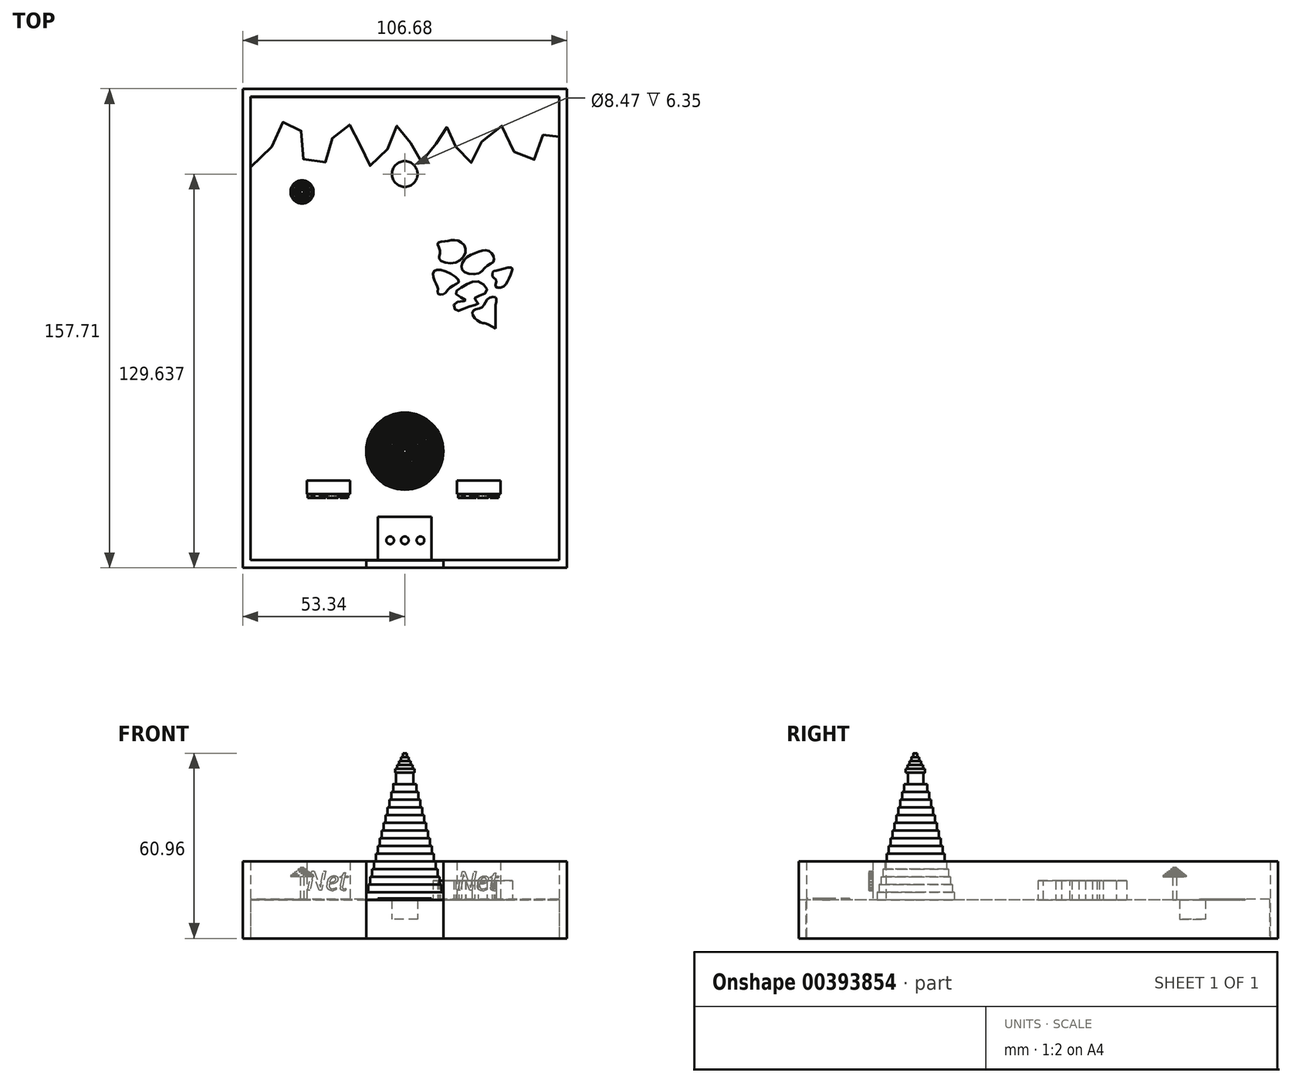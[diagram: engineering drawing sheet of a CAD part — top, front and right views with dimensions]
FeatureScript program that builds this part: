
annotation { "Feature Type Name" : "Feature", "Feature Type Description" : "" }
export const myFeature = defineFeature(function(context is Context, id is Id, definition is map)
    precondition{}
    {
        {
            var Q0;
            Q0=qCreatedBy(makeId("Top.planeOp"),FACE);
            var sketch = newSketch(context, id + "F0", { "sketchPlane" : qUnion([Q0])});
            skLineSegment(sketch, "E0.bottom", {"start": v(0, 0) * mm, "end": v(-50.8, 0) * mm});
            skLineSegment(sketch, "E0.top", {"start": v(0, -76.2) * mm, "end": v(-50.8, -76.2) * mm});
            skLineSegment(sketch, "E0.left", {"start": v(0, 0) * mm, "end": v(0, -76.2) * mm});
            skLineSegment(sketch, "E0.right", {"start": v(-50.8, 0) * mm, "end": v(-50.8, -76.2) * mm});
            skLineSegment(sketch, "E1.top", {"start": v(0, 76.2) * mm, "end": v(-50.8, 76.2) * mm});
            skLineSegment(sketch, "E1.left", {"start": v(0, 0) * mm, "end": v(0, 76.2) * mm});
            skLineSegment(sketch, "E1.right", {"start": v(-50.8, 0) * mm, "end": v(-50.8, 76.2) * mm});
            skLineSegment(sketch, "E2.bottom", {"start": v(0, 0) * mm, "end": v(50.8, 0) * mm});
            skLineSegment(sketch, "E2.top", {"start": v(0, 76.2) * mm, "end": v(50.8, 76.2) * mm});
            skLineSegment(sketch, "E2.right", {"start": v(50.8, 0) * mm, "end": v(50.8, 76.2) * mm});
            skLineSegment(sketch, "E3.top", {"start": v(0, -76.2) * mm, "end": v(50.8, -76.2) * mm});
            skLineSegment(sketch, "E3.right", {"start": v(50.8, 0) * mm, "end": v(50.8, -76.2) * mm});
            skLineSegment(sketch, "E4", {"start": v(0, 76.2) * mm, "end": v(0, -76.2) * mm, "construction": true});
            skCircle(sketch, "E5", {"center": v(0, 50.9) * mm, "radius": 4.23 * mm});
            skSolve(sketch);
        }
        {
            var Q0;
            Q0=makeQuery(id+"F0.imprint","IMPRINT",FACE,{"disambiguationData":[TD([[makeQuery(id+"F0.imprint","IMPRINT",EDGE,{"derivedFrom":sQuery(id+"F0.wireOp",EDGE,"E0.top")}),-1.0]])]});
            var Q1;
            Q1=makeQuery(id+"F0.imprint","IMPRINT",FACE,{"disambiguationData":[TD([[makeQuery(id+"F0.imprint","IMPRINT",EDGE,{"derivedFrom":sQuery(id+"F0.wireOp",EDGE,"E2.bottom")}),-1.0]])]});
            var Q2;
            {var subQ1=sQuery(id+"F0.wireOp",EDGE,"E0.bottom");Q2=makeQuery(id+"F0.imprint","IMPRINT",FACE,{"disambiguationData":[TD([[makeQuery(id+"F0.imprint","IMPRINT",EDGE,{"derivedFrom":subQ1}),-1.0]])]});}
            var Q3;
            {var subQ1=sQuery(id+"F0.wireOp",EDGE,"E2.top");Q3=makeQuery(id+"F0.imprint","IMPRINT",FACE,{"disambiguationData":[TD([[makeQuery(id+"F0.imprint","IMPRINT",EDGE,{"derivedFrom":subQ1}),-1.0]])]});}
            extrude(context, id + "F1", {"entities" : qUnion([Q0, Q1, Q2, Q3]), "depth" : 12.7 * mm});
        }
        {
            var Q0;
            Q0=makeQuery(id+"F1.opExtrude","CAP_FACE",FACE,{"disambiguationData":[OSD([sQuery(id+"F0.wireOp",EDGE,"E0.top"),sQuery(id+"F0.wireOp",EDGE,"E0.right"),sQuery(id+"F0.wireOp",EDGE,"E1.top"),sQuery(id+"F0.wireOp",EDGE,"E1.right"),sQuery(id+"F0.wireOp",EDGE,"E2.top"),sQuery(id+"F0.wireOp",EDGE,"E2.right"),sQuery(id+"F0.wireOp",EDGE,"E3.top"),sQuery(id+"F0.wireOp",EDGE,"E3.right")])],"isStart":false});
            var sketch = newSketch(context, id + "F2", { "sketchPlane" : qUnion([Q0])});
            skCircle(sketch, "E6", {"center": v(0, -40.32) * mm, "radius": 12.7 * mm});
            skSolve(sketch);
        }
        {
            var Q0;
            Q0 = qSketchRegion(id + "F2", true);
            extrude(context, id + "F3", {"entities" : qUnion([Q0]), "operationType" : NewBodyOperationType.ADD, "depth" : 2.54 * mm});
        }
        {
            var Q0;
            Q0=makeQuery(id+"F3.opExtrude","CAP_FACE",FACE,{"disambiguationData":[OSD([sQuery(id+"F2.wireOp",EDGE,"E6")])],"isStart":false});
            var sketch = newSketch(context, id + "F4", { "sketchPlane" : qUnion([Q0])});
            skCircle(sketch, "E7", {"center": v(0, -40.32) * mm, "radius": 12.07 * mm});
            skSolve(sketch);
        }
        {
            var Q0;
            Q0 = qSketchRegion(id + "F4", true);
            extrude(context, id + "F5", {"entities" : qUnion([Q0]), "operationType" : NewBodyOperationType.ADD, "depth" : 2.54 * mm});
        }
        {
            var Q0;
            Q0=makeQuery(id+"F5.opExtrude","CAP_FACE",FACE,{"disambiguationData":[OSD([sQuery(id+"F4.wireOp",EDGE,"E7")])],"isStart":false});
            var sketch = newSketch(context, id + "F6", { "sketchPlane" : qUnion([Q0])});
            skCircle(sketch, "E8", {"center": v(0, -40.32) * mm, "radius": 11.43 * mm});
            skSolve(sketch);
        }
        {
            var Q0;
            Q0 = qSketchRegion(id + "F6", true);
            extrude(context, id + "F7", {"entities" : qUnion([Q0]), "operationType" : NewBodyOperationType.ADD, "depth" : 2.54 * mm});
        }
        {
            var Q0;
            Q0=makeQuery(id+"F7.opExtrude","CAP_FACE",FACE,{"disambiguationData":[OSD([sQuery(id+"F6.wireOp",EDGE,"E8")])],"isStart":false});
            var sketch = newSketch(context, id + "F8", { "sketchPlane" : qUnion([Q0])});
            skCircle(sketch, "E9", {"center": v(0, -40.32) * mm, "radius": 10.8 * mm});
            skSolve(sketch);
        }
        {
            var Q0;
            Q0 = qSketchRegion(id + "F8", true);
            extrude(context, id + "F9", {"entities" : qUnion([Q0]), "operationType" : NewBodyOperationType.ADD, "depth" : 2.54 * mm});
        }
        {
            var Q0;
            Q0=makeQuery(id+"F9.opExtrude","CAP_FACE",FACE,{"disambiguationData":[OSD([sQuery(id+"F8.wireOp",EDGE,"E9")])],"isStart":false});
            var sketch = newSketch(context, id + "F10", { "sketchPlane" : qUnion([Q0])});
            skCircle(sketch, "E10", {"center": v(0, -40.32) * mm, "radius": 10.16 * mm});
            skSolve(sketch);
        }
        {
            var Q0;
            Q0 = qSketchRegion(id + "F10", true);
            extrude(context, id + "F11", {"entities" : qUnion([Q0]), "operationType" : NewBodyOperationType.ADD, "depth" : 2.54 * mm});
        }
        {
            var Q0;
            Q0=makeQuery(id+"F11.opExtrude","CAP_FACE",FACE,{"disambiguationData":[OSD([sQuery(id+"F10.wireOp",EDGE,"E10")])],"isStart":false});
            var sketch = newSketch(context, id + "F12", { "sketchPlane" : qUnion([Q0])});
            skCircle(sketch, "E11", {"center": v(0, -40.32) * mm, "radius": 9.53 * mm});
            skSolve(sketch);
        }
        {
            var Q0;
            Q0 = qSketchRegion(id + "F12", true);
            extrude(context, id + "F13", {"entities" : qUnion([Q0]), "operationType" : NewBodyOperationType.ADD, "depth" : 2.54 * mm});
        }
        {
            var Q0;
            Q0=makeQuery(id+"F13.opExtrude","CAP_FACE",FACE,{"disambiguationData":[OSD([sQuery(id+"F12.wireOp",EDGE,"E11")])],"isStart":false});
            var sketch = newSketch(context, id + "F14", { "sketchPlane" : qUnion([Q0])});
            skCircle(sketch, "E12", {"center": v(0, -40.32) * mm, "radius": 8.89 * mm});
            skSolve(sketch);
        }
        {
            var Q0;
            Q0 = qSketchRegion(id + "F14", true);
            extrude(context, id + "F15", {"entities" : qUnion([Q0]), "operationType" : NewBodyOperationType.ADD, "depth" : 2.54 * mm});
        }
        {
            var Q0;
            Q0=makeQuery(id+"F15.opExtrude","CAP_FACE",FACE,{"disambiguationData":[OSD([sQuery(id+"F14.wireOp",EDGE,"E12")])],"isStart":false});
            var sketch = newSketch(context, id + "F16", { "sketchPlane" : qUnion([Q0])});
            skCircle(sketch, "E13", {"center": v(0, -40.32) * mm, "radius": 8.26 * mm});
            skSolve(sketch);
        }
        {
            var Q0;
            Q0 = qSketchRegion(id + "F16", true);
            extrude(context, id + "F17", {"entities" : qUnion([Q0]), "operationType" : NewBodyOperationType.ADD, "depth" : 2.54 * mm});
        }
        {
            var Q0;
            Q0=makeQuery(id+"F17.opExtrude","CAP_FACE",FACE,{"disambiguationData":[OSD([sQuery(id+"F16.wireOp",EDGE,"E13")])],"isStart":false});
            var sketch = newSketch(context, id + "F18", { "sketchPlane" : qUnion([Q0])});
            skCircle(sketch, "E14", {"center": v(0, -40.32) * mm, "radius": 7.62 * mm});
            skSolve(sketch);
        }
        {
            var Q0;
            Q0 = qSketchRegion(id + "F18", true);
            extrude(context, id + "F19", {"entities" : qUnion([Q0]), "operationType" : NewBodyOperationType.ADD, "depth" : 2.54 * mm});
        }
        {
            var Q0;
            Q0=makeQuery(id+"F19.opExtrude","CAP_FACE",FACE,{"disambiguationData":[OSD([sQuery(id+"F18.wireOp",EDGE,"E14")])],"isStart":false});
            var sketch = newSketch(context, id + "F20", { "sketchPlane" : qUnion([Q0])});
            skCircle(sketch, "E15", {"center": v(0, -40.32) * mm, "radius": 6.99 * mm});
            skSolve(sketch);
        }
        {
            var Q0;
            Q0 = qSketchRegion(id + "F20", true);
            extrude(context, id + "F21", {"entities" : qUnion([Q0]), "operationType" : NewBodyOperationType.ADD, "depth" : 2.54 * mm});
        }
        {
            var Q0;
            Q0=makeQuery(id+"F21.opExtrude","CAP_FACE",FACE,{"disambiguationData":[OSD([sQuery(id+"F20.wireOp",EDGE,"E15")])],"isStart":false});
            var sketch = newSketch(context, id + "F22", { "sketchPlane" : qUnion([Q0])});
            skCircle(sketch, "E16", {"center": v(0, -40.32) * mm, "radius": 6.35 * mm});
            skSolve(sketch);
        }
        {
            var Q0;
            Q0 = qSketchRegion(id + "F22", true);
            extrude(context, id + "F23", {"entities" : qUnion([Q0]), "operationType" : NewBodyOperationType.ADD, "depth" : 2.54 * mm});
        }
        {
            var Q0;
            Q0=makeQuery(id+"F23.opExtrude","CAP_FACE",FACE,{"disambiguationData":[OSD([sQuery(id+"F22.wireOp",EDGE,"E16")])],"isStart":false});
            var sketch = newSketch(context, id + "F24", { "sketchPlane" : qUnion([Q0])});
            skCircle(sketch, "E17", {"center": v(0, -40.32) * mm, "radius": 5.72 * mm});
            skSolve(sketch);
        }
        {
            var Q0;
            Q0 = qSketchRegion(id + "F24", true);
            extrude(context, id + "F25", {"entities" : qUnion([Q0]), "operationType" : NewBodyOperationType.ADD, "depth" : 2.54 * mm});
        }
        {
            var Q0;
            Q0=makeQuery(id+"F25.opExtrude","CAP_FACE",FACE,{"disambiguationData":[OSD([sQuery(id+"F24.wireOp",EDGE,"E17")])],"isStart":false});
            var sketch = newSketch(context, id + "F26", { "sketchPlane" : qUnion([Q0])});
            skCircle(sketch, "E18", {"center": v(0, -40.32) * mm, "radius": 5.08 * mm});
            skSolve(sketch);
        }
        {
            var Q0;
            Q0 = qSketchRegion(id + "F26", true);
            extrude(context, id + "F27", {"entities" : qUnion([Q0]), "operationType" : NewBodyOperationType.ADD, "depth" : 2.54 * mm});
        }
        {
            var Q0;
            Q0=makeQuery(id+"F27.opExtrude","CAP_FACE",FACE,{"disambiguationData":[OSD([sQuery(id+"F26.wireOp",EDGE,"E18")])],"isStart":false});
            var sketch = newSketch(context, id + "F28", { "sketchPlane" : qUnion([Q0])});
            skCircle(sketch, "E19", {"center": v(0, -40.32) * mm, "radius": 4.45 * mm});
            skSolve(sketch);
        }
        {
            var Q0;
            Q0 = qSketchRegion(id + "F28", true);
            extrude(context, id + "F29", {"entities" : qUnion([Q0]), "operationType" : NewBodyOperationType.ADD, "depth" : 2.54 * mm});
        }
        {
            var Q0;
            Q0=makeQuery(id+"F29.opExtrude","CAP_FACE",FACE,{"disambiguationData":[OSD([sQuery(id+"F28.wireOp",EDGE,"E19")])],"isStart":false});
            var sketch = newSketch(context, id + "F30", { "sketchPlane" : qUnion([Q0])});
            skCircle(sketch, "E20", {"center": v(0, -40.32) * mm, "radius": 3.81 * mm});
            skSolve(sketch);
        }
        {
            var Q0;
            Q0 = qSketchRegion(id + "F30", true);
            extrude(context, id + "F31", {"entities" : qUnion([Q0]), "operationType" : NewBodyOperationType.ADD, "depth" : 2.54 * mm});
        }
        {
            var Q0;
            Q0=makeQuery(id+"F31.opExtrude","CAP_FACE",FACE,{"disambiguationData":[OSD([sQuery(id+"F30.wireOp",EDGE,"E20")])],"isStart":false});
            var sketch = newSketch(context, id + "F32", { "sketchPlane" : qUnion([Q0])});
            skSolve(sketch);
        }
        {
            var Q0;
            Q0=makeQuery(id+"F32.imprint","IMPRINT",FACE,{"disambiguationData":[TD([[makeQuery(id+"F32.imprint","IMPRINT",EDGE,{"derivedFrom":makeQuery(id+"F31.opExtrude","CAP_EDGE",EDGE,{"disambiguationData":[OSD([sQuery(id+"F30.wireOp",EDGE,"E20")])],"isStart":false})}),1.0]])]});
            var sketch = newSketch(context, id + "F33", { "sketchPlane" : qUnion([Q0])});
            skLineSegment(sketch, "E21.bottom", {"start": v(2.78, -37.78) * mm, "end": v(-2.9, -37.78) * mm});
            skLineSegment(sketch, "E21.top", {"start": v(2.78, -42.86) * mm, "end": v(-2.9, -42.86) * mm});
            skLineSegment(sketch, "E21.left", {"start": v(-2.9, -42.86) * mm, "end": v(-2.9, -37.78) * mm});
            skLineSegment(sketch, "E21.right", {"start": v(2.78, -42.86) * mm, "end": v(2.78, -37.78) * mm});
            skSolve(sketch);
        }
        {
            var Q0;
            Q0 = qSketchRegion(id + "F33", true);
            extrude(context, id + "F34", {"entities" : qUnion([Q0]), "operationType" : NewBodyOperationType.ADD, "depth" : 3.8 * mm});
        }
        {
            var Q0;
            Q0=makeQuery(id+"F34.opExtrude","CAP_FACE",FACE,{"disambiguationData":[OSD([sQuery(id+"F33.wireOp",EDGE,"E21.bottom"),sQuery(id+"F33.wireOp",EDGE,"E21.top"),sQuery(id+"F33.wireOp",EDGE,"E21.left"),sQuery(id+"F33.wireOp",EDGE,"E21.right")])],"isStart":false});
            var sketch = newSketch(context, id + "F35", { "sketchPlane" : qUnion([Q0])});
            skCircle(sketch, "E22", {"center": v(0, -40.36) * mm, "radius": 3.17 * mm});
            skSolve(sketch);
        }
        {
            var Q0;
            Q0 = qSketchRegion(id + "F35", true);
            extrude(context, id + "F36", {"entities" : qUnion([Q0]), "operationType" : NewBodyOperationType.ADD, "depth" : 1.27 * mm});
        }
        {
            var Q0;
            Q0=makeQuery(id+"F36.opExtrude","CAP_FACE",FACE,{"disambiguationData":[OSD([sQuery(id+"F35.wireOp",EDGE,"E22")])],"isStart":false});
            var sketch = newSketch(context, id + "F37", { "sketchPlane" : qUnion([Q0])});
            skCircle(sketch, "E23", {"center": v(0, -40.36) * mm, "radius": 2.54 * mm});
            skSolve(sketch);
        }
        {
            var Q0;
            Q0 = qSketchRegion(id + "F37", true);
            extrude(context, id + "F38", {"entities" : qUnion([Q0]), "operationType" : NewBodyOperationType.ADD, "depth" : 1.27 * mm});
        }
        {
            var Q0;
            Q0=makeQuery(id+"F38.opExtrude","CAP_FACE",FACE,{"disambiguationData":[OSD([sQuery(id+"F37.wireOp",EDGE,"E23")])],"isStart":false});
            var sketch = newSketch(context, id + "F39", { "sketchPlane" : qUnion([Q0])});
            skCircle(sketch, "E24", {"center": v(0, -40.36) * mm, "radius": 1.9 * mm});
            skSolve(sketch);
        }
        {
            var Q0;
            Q0 = qSketchRegion(id + "F39", true);
            extrude(context, id + "F40", {"entities" : qUnion([Q0]), "operationType" : NewBodyOperationType.ADD, "depth" : 1.27 * mm});
        }
        {
            var Q0;
            Q0=makeQuery(id+"F40.opExtrude","CAP_FACE",FACE,{"disambiguationData":[OSD([sQuery(id+"F39.wireOp",EDGE,"E24")])],"isStart":false});
            var sketch = newSketch(context, id + "F41", { "sketchPlane" : qUnion([Q0])});
            skCircle(sketch, "E25", {"center": v(0, -40.36) * mm, "radius": 1.27 * mm});
            skSolve(sketch);
        }
        {
            var Q0;
            Q0 = qSketchRegion(id + "F41", true);
            extrude(context, id + "F42", {"entities" : qUnion([Q0]), "operationType" : NewBodyOperationType.ADD, "depth" : 1.27 * mm});
        }
        {
            var Q0;
            Q0=makeQuery(id+"F42.opExtrude","CAP_FACE",FACE,{"disambiguationData":[OSD([sQuery(id+"F41.wireOp",EDGE,"E25")])],"isStart":false});
            var sketch = newSketch(context, id + "F43", { "sketchPlane" : qUnion([Q0])});
            skCircle(sketch, "E26", {"center": v(0, -40.36) * mm, "radius": 0.64 * mm});
            skSolve(sketch);
        }
        {
            var Q0;
            Q0 = qSketchRegion(id + "F43", true);
            extrude(context, id + "F44", {"entities" : qUnion([Q0]), "operationType" : NewBodyOperationType.ADD, "depth" : 1.27 * mm});
        }
        {
            var Q0;
            Q0=makeQuery(id+"F1.opExtrude","CAP_FACE",FACE,{"disambiguationData":[OSD([sQuery(id+"F0.wireOp",EDGE,"E0.top"),sQuery(id+"F0.wireOp",EDGE,"E0.right"),sQuery(id+"F0.wireOp",EDGE,"E1.top"),sQuery(id+"F0.wireOp",EDGE,"E1.right"),sQuery(id+"F0.wireOp",EDGE,"E2.top"),sQuery(id+"F0.wireOp",EDGE,"E2.right"),sQuery(id+"F0.wireOp",EDGE,"E3.top"),sQuery(id+"F0.wireOp",EDGE,"E3.right")])],"isStart":false});
            var sketch = newSketch(context, id + "F45", { "sketchPlane" : qUnion([Q0])});
            skLineSegment(sketch, "E27", {"start": v(0, 76.2) * mm, "end": v(0, -76.2) * mm, "construction": true});
            skFitSpline(sketch, "E28", {"points": [v(-50.8, 53.13) * mm, v(-46.3, 55.4) * mm, v(-43.92, 59.48) * mm, v(-42.63, 64.05) * mm, v(-41.24, 67.32) * mm, v(-37.86, 68.21) * mm, v(-35.48, 67.42) * mm, v(-34.29, 65.84) * mm, v(-34, 60.9) * mm, v(-33.8, 58.05) * mm, v(-32.52, 54.2) * mm, v(-28.97, 53.62) * mm, v(-26.2, 54.7) * mm, v(-25.02, 57.96) * mm, v(-24.33, 60.93) * mm, v(-23.43, 64.2) * mm, v(-21.55, 66.88) * mm, v(-18.37, 67.18) * mm, v(-16.29, 65.9) * mm, v(-15, 63.3) * mm, v(-14.7, 59.64) * mm, v(-14.6, 56.06) * mm, v(-12.22, 53.78) * mm, v(-8.74, 54.08) * mm, v(-6.26, 56.66) * mm, v(-5.57, 60.83) * mm, v(-5.37, 64.7) * mm, v(-2.4, 66.78) * mm, v(0.79, 65.6) * mm, v(1.68, 63.01) * mm, v(2.18, 59.24) * mm, v(2.77, 56.36) * mm, v(5.05, 54.97) * mm, v(8.53, 55.77) * mm, v(10.12, 58.55) * mm, v(10.31, 62.71) * mm, v(10.61, 65.6) * mm, v(13.1, 66.29) * mm, v(15.87, 65.7) * mm, v(16.37, 63.01) * mm, v(16.87, 59.24) * mm, v(18.06, 55.96) * mm, v(20.84, 54.48) * mm, v(23.42, 55.67) * mm, v(24.7, 58.74) * mm, v(25.3, 61.42) * mm, v(26.9, 65.2) * mm, v(30.76, 66.98) * mm, v(34.63, 64.4) * mm, v(35.53, 59.94) * mm, v(37.31, 55.96) * mm, v(40.1, 53.98) * mm, v(43.47, 56.86) * mm, v(44.96, 60.83) * mm, v(45.35, 63.11) * mm, v(46.84, 65.8) * mm, v(49.03, 65.6) * mm, v(50.8, 63.21) * mm, v(50.8, 63.11) * mm], "startDerivative": vector(234.29, 84.66) * mm, "endDerivative": vector(-8.09, -21.2) * mm});
            skCircle(sketch, "E29", {"center": v(0, 50.69) * mm, "radius": 4.23 * mm});
            skSolve(sketch);
        }
        {
            var Q0;
            {var subQ5=makeQuery(id+"F1.opExtrude","CAP_EDGE",EDGE,{"disambiguationData":[OSD([sQuery(id+"F0.wireOp",EDGE,"E1.top"),sQuery(id+"F0.wireOp",EDGE,"E2.top")])],"isStart":false});Q0=makeQuery(id+"F45.imprint","IMPRINT",FACE,{"disambiguationData":[TD([[makeQuery(id+"F45.imprint","IMPRINT",EDGE,{"derivedFrom":subQ5}),1.0]])]});}
            extrude(context, id + "F46", {"entities" : qUnion([Q0]), "operationType" : NewBodyOperationType.ADD, "depth" : 0.25 * mm});
        }
        {
            var Q0;
            {var subQ0=sQuery(id+"F0.wireOp",EDGE,"E5");var subQ1=sQuery(id+"F0.wireOp",EDGE,"E1.left");var subQ2=makeQuery(id+"F0.imprint","INTERSECT",VERTEX,{"disambiguationData":[OD(0.0)],"derivedFrom":[subQ1,subQ0]});Q0=makeQuery(id+"F0.imprint","IMPRINT",FACE,{"disambiguationData":[TD([[makeQuery(id+"F0.imprint","IMPRINT",EDGE,{"disambiguationData":[TD([[subQ2,-1.0]])],"derivedFrom":subQ1}),1.0]])]});}
            var Q1;
            {var subQ0=sQuery(id+"F0.wireOp",EDGE,"E5");var subQ1=sQuery(id+"F0.wireOp",EDGE,"E1.left");var subQ2=makeQuery(id+"F0.imprint","INTERSECT",VERTEX,{"disambiguationData":[OD(0.0)],"derivedFrom":[subQ1,subQ0]});Q1=makeQuery(id+"F0.imprint","IMPRINT",FACE,{"disambiguationData":[TD([[makeQuery(id+"F0.imprint","IMPRINT",EDGE,{"disambiguationData":[TD([[subQ2,-1.0]])],"derivedFrom":subQ1}),-1.0]])]});}
            extrude(context, id + "F47", {"entities" : qUnion([Q0, Q1]), "operationType" : NewBodyOperationType.ADD, "depth" : 6.35 * mm});
        }
        {
            var Q0;
            Q0=makeQuery(id+"F1.opExtrude","CAP_FACE",FACE,{"disambiguationData":[OSD([sQuery(id+"F0.wireOp",EDGE,"E0.top"),sQuery(id+"F0.wireOp",EDGE,"E0.right"),sQuery(id+"F0.wireOp",EDGE,"E1.top"),sQuery(id+"F0.wireOp",EDGE,"E1.right"),sQuery(id+"F0.wireOp",EDGE,"E2.top"),sQuery(id+"F0.wireOp",EDGE,"E2.right"),sQuery(id+"F0.wireOp",EDGE,"E3.top"),sQuery(id+"F0.wireOp",EDGE,"E3.right"),sQuery(id+"F0.wireOp",EDGE,"E5")])],"isStart":false});
            var sketch = newSketch(context, id + "F48", { "sketchPlane" : qUnion([Q0])});
            skLineSegment(sketch, "E30.bottom", {"start": v(-18.02, -50.04) * mm, "end": v(-32.28, -50.04) * mm});
            skLineSegment(sketch, "E30.top", {"start": v(-18.02, -54.41) * mm, "end": v(-32.28, -54.41) * mm});
            skLineSegment(sketch, "E30.left", {"start": v(-18.02, -50.04) * mm, "end": v(-18.02, -54.41) * mm});
            skLineSegment(sketch, "E30.right", {"start": v(-32.28, -50.04) * mm, "end": v(-32.28, -54.41) * mm});
            skSolve(sketch);
        }
        {
            var Q0;
            Q0 = qSketchRegion(id + "F48", true);
            extrude(context, id + "F49", {"entities" : qUnion([Q0]), "operationType" : NewBodyOperationType.ADD, "depth" : 12.7 * mm});
        }
        {
            var Q0;
            Q0=makeQuery(id+"F49.opExtrude","SWEPT_FACE",FACE,{"disambiguationData":[OSD([sQuery(id+"F48.wireOp",EDGE,"E30.top")])]});
            var sketch = newSketch(context, id + "F50", { "sketchPlane" : qUnion([Q0])});
            skText(sketch, "E31", { "text": "Net", "fontName": "OpenSans-Italic.ttf"});
            const initialGuessF50  = {"E31": [-0.03228, 0.01583, 1, 0, 0.00635]};
            skSetInitialGuess(sketch, initialGuessF50);
            skSolve(sketch);
        }
        {
            var Q0;
            Q0 = qSketchRegion(id + "F50", true);
            extrude(context, id + "F51", {"entities" : qUnion([Q0]), "operationType" : NewBodyOperationType.ADD, "depth" : 1.27 * mm});
        }
        {
            var Q0;
            Q0=makeQuery(id+"F1.opExtrude","CAP_FACE",FACE,{"disambiguationData":[OSD([sQuery(id+"F0.wireOp",EDGE,"E0.top"),sQuery(id+"F0.wireOp",EDGE,"E0.right"),sQuery(id+"F0.wireOp",EDGE,"E1.top"),sQuery(id+"F0.wireOp",EDGE,"E1.right"),sQuery(id+"F0.wireOp",EDGE,"E2.top"),sQuery(id+"F0.wireOp",EDGE,"E2.right"),sQuery(id+"F0.wireOp",EDGE,"E3.top"),sQuery(id+"F0.wireOp",EDGE,"E3.right"),sQuery(id+"F0.wireOp",EDGE,"E5")])],"isStart":false});
            var sketch = newSketch(context, id + "F52", { "sketchPlane" : qUnion([Q0])});
            skLineSegment(sketch, "E32.bottom", {"start": v(17.23, -50.04) * mm, "end": v(31.49, -50.04) * mm});
            skLineSegment(sketch, "E32.top", {"start": v(17.23, -54.41) * mm, "end": v(31.49, -54.41) * mm});
            skLineSegment(sketch, "E32.left", {"start": v(17.23, -50.04) * mm, "end": v(17.23, -54.41) * mm});
            skLineSegment(sketch, "E32.right", {"start": v(31.49, -50.04) * mm, "end": v(31.49, -54.41) * mm});
            skSolve(sketch);
        }
        {
            var Q0;
            Q0 = qSketchRegion(id + "F52", true);
            extrude(context, id + "F53", {"entities" : qUnion([Q0]), "operationType" : NewBodyOperationType.ADD, "depth" : 12.7 * mm});
        }
        {
            var Q0;
            Q0=makeQuery(id+"F53.opExtrude","SWEPT_FACE",FACE,{"disambiguationData":[OSD([sQuery(id+"F52.wireOp",EDGE,"E32.top")])]});
            var sketch = newSketch(context, id + "F54", { "sketchPlane" : qUnion([Q0])});
            skText(sketch, "E33", { "text": "Net", "fontName": "OpenSans-Italic.ttf"});
            const initialGuessF54  = {"E33": [0.01723, 0.01577, 1, 0, 0.00635]};
            skSetInitialGuess(sketch, initialGuessF54);
            skSolve(sketch);
        }
        {
            var Q0;
            Q0 = qSketchRegion(id + "F54", true);
            extrude(context, id + "F55", {"entities" : qUnion([Q0]), "operationType" : NewBodyOperationType.ADD, "depth" : 1.27 * mm});
        }
        {
            var Q0;
            Q0=makeQuery(id+"F1.opExtrude","CAP_FACE",FACE,{"disambiguationData":[OSD([sQuery(id+"F0.wireOp",EDGE,"E0.top"),sQuery(id+"F0.wireOp",EDGE,"E0.right"),sQuery(id+"F0.wireOp",EDGE,"E1.top"),sQuery(id+"F0.wireOp",EDGE,"E1.right"),sQuery(id+"F0.wireOp",EDGE,"E2.top"),sQuery(id+"F0.wireOp",EDGE,"E2.right"),sQuery(id+"F0.wireOp",EDGE,"E3.top"),sQuery(id+"F0.wireOp",EDGE,"E3.right"),sQuery(id+"F0.wireOp",EDGE,"E5")])],"isStart":false});
            var sketch = newSketch(context, id + "F56", { "sketchPlane" : qUnion([Q0])});
            skLineSegment(sketch, "E34", {"start": v(29.9, 7.72) * mm, "end": v(29.9, 0) * mm});
            skFitSpline(sketch, "E35", {"points": [v(29.9, 0) * mm, v(26.34, 1.78) * mm, v(25.75, 1.78) * mm, v(22.78, 3.76) * mm, v(22.58, 5.94) * mm, v(25.55, 7.13) * mm, v(27.33, 9.7) * mm, v(29.9, 10.3) * mm, v(29.9, 7.72) * mm], "startDerivative": vector(-28.75, 16.45) * mm, "endDerivative": vector(-6.2, -26.3) * mm});
            skSolve(sketch);
        }
        {
            var Q0;
            Q0 = qSketchRegion(id + "F56", true);
            extrude(context, id + "F57", {"entities" : qUnion([Q0]), "operationType" : NewBodyOperationType.ADD, "depth" : 6.35 * mm});
        }
        {
            var Q0;
            Q0=makeQuery(id+"F1.opExtrude","CAP_FACE",FACE,{"disambiguationData":[OSD([sQuery(id+"F0.wireOp",EDGE,"E0.top"),sQuery(id+"F0.wireOp",EDGE,"E0.right"),sQuery(id+"F0.wireOp",EDGE,"E1.top"),sQuery(id+"F0.wireOp",EDGE,"E1.right"),sQuery(id+"F0.wireOp",EDGE,"E2.top"),sQuery(id+"F0.wireOp",EDGE,"E2.right"),sQuery(id+"F0.wireOp",EDGE,"E3.top"),sQuery(id+"F0.wireOp",EDGE,"E3.right"),sQuery(id+"F0.wireOp",EDGE,"E5")])],"isStart":false});
            var sketch = newSketch(context, id + "F58", { "sketchPlane" : qUnion([Q0])});
            skFitSpline(sketch, "E36", {"points": [v(21.2, 7.33) * mm, v(17.03, 5.94) * mm, v(16.44, 8.32) * mm, v(20, 9.3) * mm, v(16.83, 11.49) * mm, v(19.21, 13.86) * mm, v(24.36, 15.45) * mm, v(26.93, 12.08) * mm, v(22.97, 9.9) * mm, v(24.16, 8.32) * mm, v(21.2, 7.33) * mm]});
            skFitSpline(sketch, "E37", {"points": [v(29.9, 13.86) * mm, v(32.48, 13.86) * mm, v(34.46, 17.03) * mm, v(35.25, 20) * mm, v(30.5, 19.21) * mm, v(29.11, 18.81) * mm, v(28.91, 17.23) * mm, v(30.1, 15.84) * mm, v(29.9, 13.86) * mm]});
            skFitSpline(sketch, "E38", {"points": [v(24.36, 18.22) * mm, v(26.93, 20.6) * mm, v(29.11, 21.98) * mm, v(29.11, 23.96) * mm, v(27.13, 25.75) * mm, v(24.36, 25.35) * mm, v(20.6, 23.57) * mm, v(18.81, 21.2) * mm, v(19.4, 18.81) * mm, v(24.36, 18.22) * mm]});
            skFitSpline(sketch, "E39", {"points": [v(13.47, 18.81) * mm, v(17.82, 15.45) * mm, v(15.05, 13.67) * mm, v(13.07, 11.49) * mm, v(10.9, 11.49) * mm, v(10.9, 13.27) * mm, v(9.9, 15.45) * mm, v(9.5, 18.81) * mm, v(13.47, 18.81) * mm]});
            skFitSpline(sketch, "E40", {"points": [v(11.29, 22.97) * mm, v(16.83, 21.78) * mm, v(20, 26.54) * mm, v(16.83, 29.11) * mm, v(13.47, 28.72) * mm, v(10.9, 28.12) * mm, v(11.68, 25.15) * mm, v(11.29, 22.97) * mm]});
            skSolve(sketch);
        }
        {
            var Q0;
            Q0 = qSketchRegion(id + "F58", true);
            extrude(context, id + "F59", {"entities" : qUnion([Q0]), "operationType" : NewBodyOperationType.ADD, "depth" : 6.35 * mm});
        }
        {
            var Q0;
            Q0=qCreatedBy(makeId("Top.planeOp"),FACE);
            var sketch = newSketch(context, id + "F60", { "sketchPlane" : qUnion([Q0])});
            skLineSegment(sketch, "E41.left", {"start": v(50.8, -76.2) * mm, "end": v(50.8, -78.74) * mm});
            skLineSegment(sketch, "E41.right", {"start": v(-50.8, -76.2) * mm, "end": v(-50.8, -78.74) * mm});
            skPoint(sketch, "E42.firstSnap0", {"position": v(50.8, -6.5) * mm});
            skLineSegment(sketch, "E42.bottom", {"start": v(50.8, 76.43) * mm, "end": v(-50.8, 76.43) * mm});
            skLineSegment(sketch, "E42.top", {"start": v(50.8, 78.97) * mm, "end": v(-50.8, 78.97) * mm});
            skLineSegment(sketch, "E42.left", {"start": v(50.8, 76.43) * mm, "end": v(50.8, 78.97) * mm});
            skLineSegment(sketch, "E42.right", {"start": v(-50.8, 76.43) * mm, "end": v(-50.8, 78.97) * mm});
            skLineSegment(sketch, "E43.bottom", {"start": v(-50.8, 78.97) * mm, "end": v(-53.34, 78.97) * mm});
            skLineSegment(sketch, "E43.top", {"start": v(-50.8, -78.74) * mm, "end": v(-53.34, -78.74) * mm});
            skLineSegment(sketch, "E43.left", {"start": v(-50.8, 78.97) * mm, "end": v(-50.8, -78.74) * mm});
            skLineSegment(sketch, "E43.right", {"start": v(-53.34, 78.97) * mm, "end": v(-53.34, -78.74) * mm});
            skLineSegment(sketch, "E44.bottom", {"start": v(50.8, 78.97) * mm, "end": v(53.34, 78.97) * mm});
            skLineSegment(sketch, "E44.top", {"start": v(50.8, -78.74) * mm, "end": v(53.34, -78.74) * mm});
            skLineSegment(sketch, "E44.left", {"start": v(50.8, 78.97) * mm, "end": v(50.8, -78.74) * mm});
            skLineSegment(sketch, "E44.right", {"start": v(53.34, 78.97) * mm, "end": v(53.34, -78.74) * mm});
            skLineSegment(sketch, "E45.bottom", {"start": v(-50.8, -76.2) * mm, "end": v(-12.7, -76.2) * mm});
            skLineSegment(sketch, "E45.top", {"start": v(-50.8, -78.74) * mm, "end": v(-12.7, -78.74) * mm});
            skLineSegment(sketch, "E45.right", {"start": v(-12.7, -76.2) * mm, "end": v(-12.7, -78.74) * mm});
            skLineSegment(sketch, "E46.bottom", {"start": v(50.8, -76.2) * mm, "end": v(12.7, -76.2) * mm});
            skLineSegment(sketch, "E46.top", {"start": v(50.8, -78.74) * mm, "end": v(12.7, -78.74) * mm});
            skLineSegment(sketch, "E46.right", {"start": v(12.7, -76.2) * mm, "end": v(12.7, -78.74) * mm});
            skSolve(sketch);
        }
        {
            var Q0;
            {var subQ0=sQuery(id+"F60.wireOp",EDGE,"E42.bottom");Q0=makeQuery(id+"F60.imprint","IMPRINT",FACE,{"disambiguationData":[TD([[makeQuery(id+"F60.imprint","IMPRINT",EDGE,{"derivedFrom":subQ0}),-1.0]])]});}
            var Q1;
            {var subQ3=sQuery(id+"F60.wireOp",EDGE,"E43.bottom");Q1=makeQuery(id+"F60.imprint","IMPRINT",FACE,{"disambiguationData":[TD([[makeQuery(id+"F60.imprint","IMPRINT",EDGE,{"derivedFrom":subQ3}),1.0]])]});}
            var Q2;
            {var subQ3=sQuery(id+"F60.wireOp",EDGE,"E44.bottom");Q2=makeQuery(id+"F60.imprint","IMPRINT",FACE,{"disambiguationData":[TD([[makeQuery(id+"F60.imprint","IMPRINT",EDGE,{"derivedFrom":subQ3}),-1.0]])]});}
            var Q3;
            {var subQ0=sQuery(id+"F60.wireOp",EDGE,"E41.bottom");Q3=makeQuery(id+"F60.imprint","IMPRINT",FACE,{"disambiguationData":[TD([[makeQuery(id+"F60.imprint","IMPRINT",EDGE,{"derivedFrom":subQ0}),1.0]])]});}
            var Q4;
            Q4=makeQuery(id+"F60.imprint","IMPRINT",FACE,{"disambiguationData":[TD([[makeQuery(id+"F60.imprint","IMPRINT",EDGE,{"derivedFrom":sQuery(id+"F60.wireOp",EDGE,"E45.bottom")}),-1.0]])]});
            var Q5;
            Q5=makeQuery(id+"F60.imprint","IMPRINT",FACE,{"disambiguationData":[TD([[makeQuery(id+"F60.imprint","IMPRINT",EDGE,{"derivedFrom":sQuery(id+"F60.wireOp",EDGE,"E46.bottom")}),1.0]])]});
            extrude(context, id + "F61", {"entities" : qUnion([Q0, Q1, Q2, Q3, Q4, Q5]), "operationType" : NewBodyOperationType.ADD, "depth" : 25.4 * mm});
        }
        {
            var Q0;
            Q0=makeQuery(id+"F1.opExtrude","CAP_FACE",FACE,{"disambiguationData":[OSD([sQuery(id+"F0.wireOp",EDGE,"E0.top"),sQuery(id+"F0.wireOp",EDGE,"E0.right"),sQuery(id+"F0.wireOp",EDGE,"E1.top"),sQuery(id+"F0.wireOp",EDGE,"E1.right"),sQuery(id+"F0.wireOp",EDGE,"E2.top"),sQuery(id+"F0.wireOp",EDGE,"E2.right"),sQuery(id+"F0.wireOp",EDGE,"E3.top"),sQuery(id+"F0.wireOp",EDGE,"E3.right"),sQuery(id+"F0.wireOp",EDGE,"E5")])],"isStart":false});
            var sketch = newSketch(context, id + "F62", { "sketchPlane" : qUnion([Q0])});
            skLineSegment(sketch, "E47.bottom", {"start": v(-8.87, -61.94) * mm, "end": v(8.73, -61.94) * mm});
            skLineSegment(sketch, "E47.top", {"start": v(-8.87, -76.2) * mm, "end": v(8.73, -76.2) * mm});
            skLineSegment(sketch, "E47.left", {"start": v(-8.87, -61.94) * mm, "end": v(-8.87, -76.2) * mm});
            skLineSegment(sketch, "E47.right", {"start": v(8.73, -61.94) * mm, "end": v(8.73, -76.2) * mm});
            skCircle(sketch, "E48", {"center": v(0, -69.68) * mm, "radius": 1.27 * mm});
            skCircle(sketch, "E49", {"center": v(5.16, -69.68) * mm, "radius": 1.27 * mm});
            skCircle(sketch, "E50", {"center": v(-4.82, -69.68) * mm, "radius": 1.27 * mm});
            skSolve(sketch);
        }
        {
            var Q0;
            Q0=makeQuery(id+"F62.imprint","IMPRINT",FACE,{"disambiguationData":[TD([[makeQuery(id+"F62.imprint","IMPRINT",EDGE,{"derivedFrom":sQuery(id+"F62.wireOp",EDGE,"E47.bottom")}),-1.0]])]});
            extrude(context, id + "F63", {"entities" : qUnion([Q0]), "operationType" : NewBodyOperationType.ADD, "depth" : 0.5 * mm});
        }
        {
            var Q0;
            {var subQ0=sQuery(id+"F0.wireOp",EDGE,"E5");var subQ1=sQuery(id+"F0.wireOp",EDGE,"E3.top");var subQ2=sQuery(id+"F0.wireOp",EDGE,"E0.top");Q0=makeQuery(id+"F63.boolean.opBoolean","SPLIT",FACE,{"disambiguationData":[TD([makeQuery(id+"F1.opExtrude","SWEPT_FACE",FACE,{"disambiguationData":[OSD([subQ0])]})])],"derivedFrom":makeQuery(id+"F1.opExtrude","CAP_FACE",FACE,{"disambiguationData":[OSD([subQ2,sQuery(id+"F0.wireOp",EDGE,"E0.right"),sQuery(id+"F0.wireOp",EDGE,"E1.top"),sQuery(id+"F0.wireOp",EDGE,"E1.right"),sQuery(id+"F0.wireOp",EDGE,"E2.top"),sQuery(id+"F0.wireOp",EDGE,"E2.right"),subQ1,sQuery(id+"F0.wireOp",EDGE,"E3.right"),subQ0])],"isStart":false})});}
            var sketch = newSketch(context, id + "F64", { "sketchPlane" : qUnion([Q0])});
            skCircle(sketch, "E51", {"center": v(-33.81, 45) * mm, "radius": 0.64 * mm});
            skSolve(sketch);
        }
        {
            var Q0;
            Q0 = qSketchRegion(id + "F64", true);
            extrude(context, id + "F65", {"entities" : qUnion([Q0]), "operationType" : NewBodyOperationType.ADD, "depth" : 7.62 * mm});
        }
        {
            var Q0;
            Q0=makeQuery(id+"F65.opExtrude","CAP_FACE",FACE,{"disambiguationData":[OSD([sQuery(id+"F64.wireOp",EDGE,"E51")])],"isStart":false});
            var sketch = newSketch(context, id + "F66", { "sketchPlane" : qUnion([Q0])});
            skCircle(sketch, "E52", {"center": v(-33.81, 45) * mm, "radius": 3.8 * mm});
            skSolve(sketch);
        }
        {
            var Q0;
            Q0 = qSketchRegion(id + "F66", true);
            extrude(context, id + "F67", {"entities" : qUnion([Q0]), "operationType" : NewBodyOperationType.ADD, "depth" : 0.5 * mm});
        }
        {
            var Q0;
            Q0=makeQuery(id+"F67.opExtrude","CAP_FACE",FACE,{"disambiguationData":[OSD([sQuery(id+"F66.wireOp",EDGE,"E52")])],"isStart":false});
            var sketch = newSketch(context, id + "F68", { "sketchPlane" : qUnion([Q0])});
            skCircle(sketch, "E53", {"center": v(-33.81, 45) * mm, "radius": 3.17 * mm});
            skSolve(sketch);
        }
        {
            var Q0;
            Q0 = qSketchRegion(id + "F68", true);
            extrude(context, id + "F69", {"entities" : qUnion([Q0]), "operationType" : NewBodyOperationType.ADD, "depth" : 0.5 * mm});
        }
        {
            var Q0;
            Q0=makeQuery(id+"F69.opExtrude","CAP_FACE",FACE,{"disambiguationData":[OSD([sQuery(id+"F68.wireOp",EDGE,"E53")])],"isStart":false});
            var sketch = newSketch(context, id + "F70", { "sketchPlane" : qUnion([Q0])});
            skCircle(sketch, "E54", {"center": v(-33.81, 45) * mm, "radius": 2.54 * mm});
            skSolve(sketch);
        }
        {
            var Q0;
            Q0 = qSketchRegion(id + "F70", true);
            extrude(context, id + "F71", {"entities" : qUnion([Q0]), "operationType" : NewBodyOperationType.ADD, "depth" : 0.5 * mm});
        }
        {
            var Q0;
            Q0=makeQuery(id+"F71.opExtrude","CAP_FACE",FACE,{"disambiguationData":[OSD([sQuery(id+"F70.wireOp",EDGE,"E54")])],"isStart":false});
            var sketch = newSketch(context, id + "F72", { "sketchPlane" : qUnion([Q0])});
            skCircle(sketch, "E55", {"center": v(-33.81, 45) * mm, "radius": 1.9 * mm});
            skSolve(sketch);
        }
        {
            var Q0;
            Q0 = qSketchRegion(id + "F72", true);
            extrude(context, id + "F73", {"entities" : qUnion([Q0]), "operationType" : NewBodyOperationType.ADD, "depth" : 0.5 * mm});
        }
        {
            var Q0;
            Q0=makeQuery(id+"F73.opExtrude","CAP_FACE",FACE,{"disambiguationData":[OSD([sQuery(id+"F72.wireOp",EDGE,"E55")])],"isStart":false});
            var sketch = newSketch(context, id + "F74", { "sketchPlane" : qUnion([Q0])});
            skCircle(sketch, "E56", {"center": v(-33.81, 45) * mm, "radius": 1.27 * mm});
            skSolve(sketch);
        }
        {
            var Q0;
            Q0 = qSketchRegion(id + "F74", true);
            extrude(context, id + "F75", {"entities" : qUnion([Q0]), "operationType" : NewBodyOperationType.ADD, "depth" : 0.5 * mm});
        }
        {
            var Q0;
            Q0=makeQuery(id+"F75.opExtrude","CAP_FACE",FACE,{"disambiguationData":[OSD([sQuery(id+"F74.wireOp",EDGE,"E56")])],"isStart":false});
            var sketch = newSketch(context, id + "F76", { "sketchPlane" : qUnion([Q0])});
            skCircle(sketch, "E57", {"center": v(-33.81, 45) * mm, "radius": 0.64 * mm});
            skSolve(sketch);
        }
        {
            var Q0;
            Q0 = qSketchRegion(id + "F76", true);
            extrude(context, id + "F77", {"entities" : qUnion([Q0]), "operationType" : NewBodyOperationType.ADD, "depth" : 0.5 * mm});
        }
        {
            var Q0;
            Q0=qCreatedBy(makeId("Top.planeOp"),FACE);
            var sketch = newSketch(context, id + "F78", { "sketchPlane" : qUnion([Q0])});
            skLineSegment(sketch, "E58.bottom", {"start": v(-12.72, -76.33) * mm, "end": v(12.68, -76.33) * mm});
            skLineSegment(sketch, "E58.top", {"start": v(-12.72, -78.69) * mm, "end": v(12.68, -78.69) * mm});
            skLineSegment(sketch, "E58.left", {"start": v(-12.72, -76.33) * mm, "end": v(-12.72, -78.69) * mm});
            skLineSegment(sketch, "E58.right", {"start": v(12.68, -76.33) * mm, "end": v(12.68, -78.69) * mm});
            skSolve(sketch);
        }
        {
            var Q0;
            Q0 = qSketchRegion(id + "F78", true);
            extrude(context, id + "F79", {"entities" : qUnion([Q0]), "operationType" : NewBodyOperationType.ADD, "depth" : 12.7 * mm});
        }
    });
